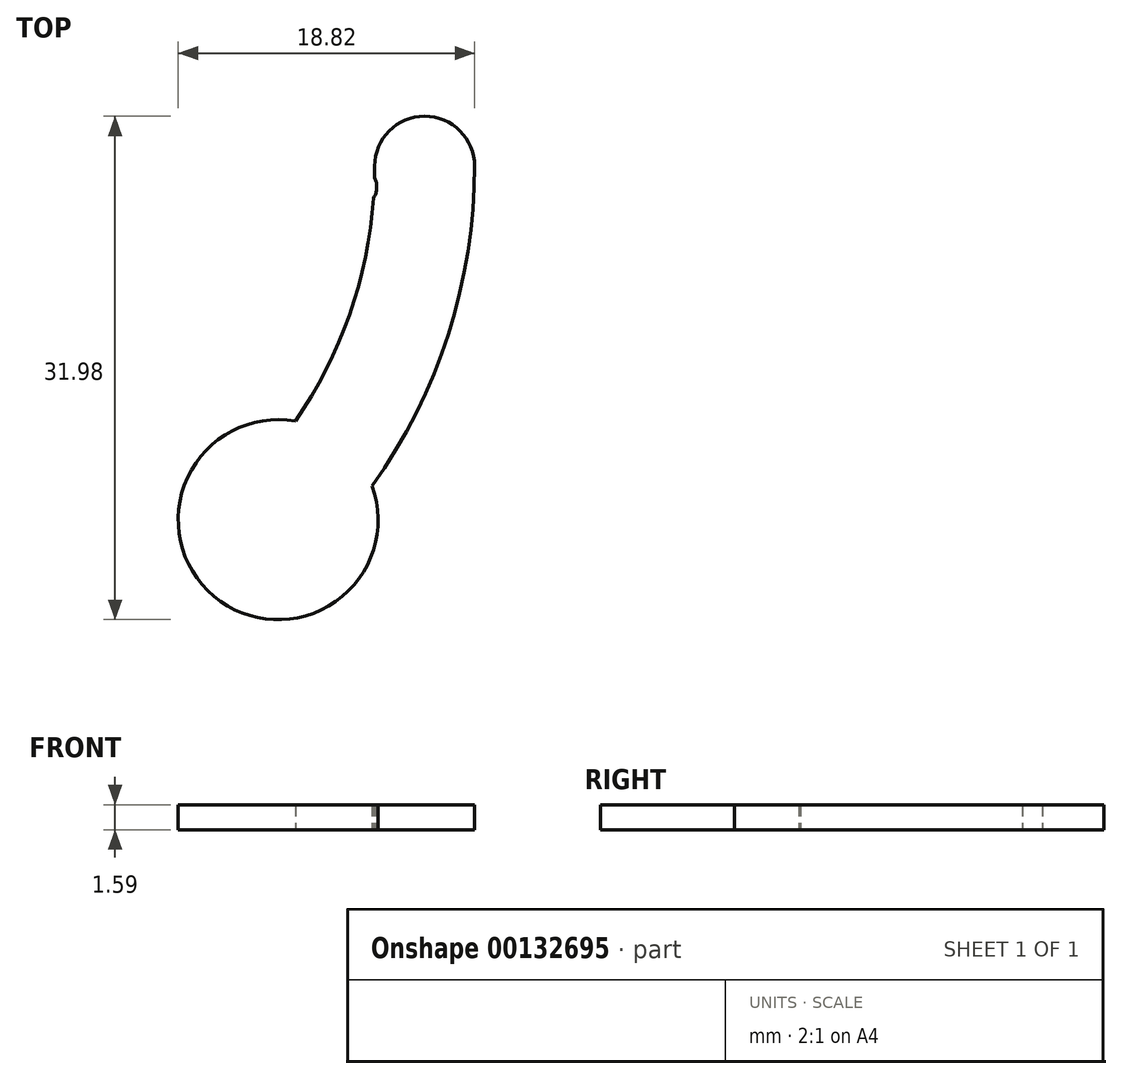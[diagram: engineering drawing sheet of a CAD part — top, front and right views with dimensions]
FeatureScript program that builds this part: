
annotation { "Feature Type Name" : "Feature", "Feature Type Description" : "" }
export const myFeature = defineFeature(function(context is Context, id is Id, definition is map)
    precondition{}
    {
        {
            var Q0;
            Q0=qCreatedBy(makeId("Top.planeOp"),FACE);
            var sketch = newSketch(context, id + "F0", { "sketchPlane" : qUnion([Q0])});
            skCircle(sketch, "E0", {"center": v(0, 0) * mm, "radius": 44.45 * mm});
            skLineSegment(sketch, "E1", {"start": v(0, 72.68) * mm, "end": v(0, -70.78) * mm});
            skLineSegment(sketch, "E2", {"start": v(70.46, 0) * mm, "end": v(34.93, 0) * mm});
            skArc(sketch, "E3", {"start": v(-34.92, 0) * mm, "mid": v(-31.75, -3.18) * mm, "end": v(-28.57, 0) * mm});
            skLineSegment(sketch, "E4.trimOffspring", {"start": v(-34.92, 0) * mm, "end": v(-64.18, 0) * mm});
            skArc(sketch, "E5.MirrorC", {"start": v(28.57, 0) * mm, "mid": v(31.75, 3.17) * mm, "end": v(34.92, 0) * mm});
            skArc(sketch, "E6", {"start": v(-23.54, 16.2) * mm, "mid": v(-26.97, 9.44) * mm, "end": v(-28.5, 2.01) * mm});
            skArc(sketch, "E7", {"start": v(-28.42, 20.3) * mm, "mid": v(-33.26, 10.66) * mm, "end": v(-34.92, 0) * mm});
            skArc(sketch, "E8.MirrorC", {"start": v(-23.54, 16.2) * mm, "mid": v(-18.37, 27.31) * mm, "end": v(-28.42, 20.3) * mm});
            skArc(sketch, "E9.MirrorC", {"start": v(23.54, -16.2) * mm, "mid": v(18.37, -27.31) * mm, "end": v(28.42, -20.3) * mm});
            skArc(sketch, "E10.trimOffspring", {"start": v(28.42, -20.3) * mm, "mid": v(33.26, -10.66) * mm, "end": v(34.92, 0) * mm});
            skArc(sketch, "E11.trimOffspring", {"start": v(23.54, -16.2) * mm, "mid": v(26.97, -9.44) * mm, "end": v(28.5, -2.01) * mm});
            skArc(sketch, "E12", {"start": v(-28.5, 2.01) * mm, "mid": v(-28.7, 1.38) * mm, "end": v(-28.57, 0.73) * mm});
            skArc(sketch, "E13.MirrorC", {"start": v(28.5, -2.01) * mm, "mid": v(28.7, -1.38) * mm, "end": v(28.57, -0.73) * mm});
            skArc(sketch, "E14.trimOffspring", {"start": v(-28.57, 0.73) * mm, "mid": v(-28.57, 0.36) * mm, "end": v(-28.58, 0) * mm});
            skArc(sketch, "E15.trimOffspring", {"start": v(28.57, -0.73) * mm, "mid": v(28.57, -0.36) * mm, "end": v(28.57, 0) * mm});
            skSolve(sketch);
        }
        {
            var Q0;
            Q0=makeQuery(id+"F0.imprint","IMPRINT",FACE,{"disambiguationData":[TD([[makeQuery(id+"F0.imprint","IMPRINT",EDGE,{"derivedFrom":sQuery(id+"F0.wireOp",EDGE,"E5.MirrorC")}),1.0]])]});
            extrude(context, id + "F1", {"entities" : qUnion([Q0]), "depth" : 1.59 * mm});
        }
    });
